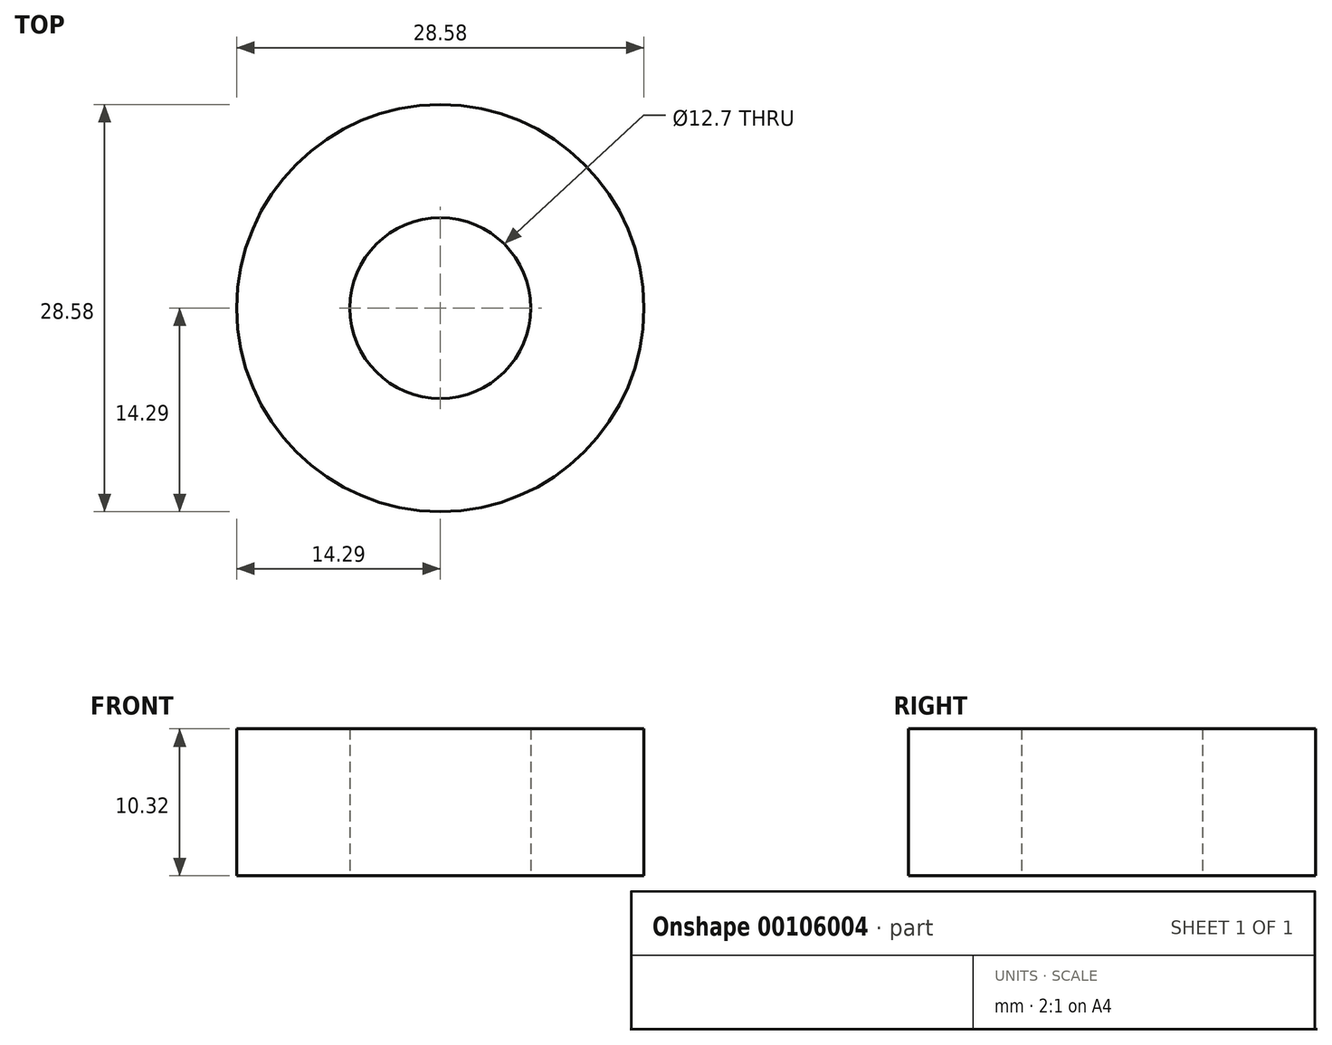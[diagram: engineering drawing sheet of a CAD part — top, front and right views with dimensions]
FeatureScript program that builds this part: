
annotation { "Feature Type Name" : "Feature", "Feature Type Description" : "" }
export const myFeature = defineFeature(function(context is Context, id is Id, definition is map)
    precondition{}
    {
        {
            var Q0;
            Q0=qCreatedBy(makeId("Top.planeOp"),FACE);
            var sketch = newSketch(context, id + "F0", { "sketchPlane" : qUnion([Q0])});
            skCircle(sketch, "E0", {"center": v(0, 0) * mm, "radius": 6.35 * mm});
            skCircle(sketch, "E1", {"center": v(0, 0) * mm, "radius": 14.29 * mm});
            skSolve(sketch);
        }
        {
            var Q0;
            Q0=makeQuery(id+"F0.imprint","IMPRINT",FACE,{"disambiguationData":[TD([[makeQuery(id+"F0.imprint","IMPRINT",EDGE,{"derivedFrom":sQuery(id+"F0.wireOp",EDGE,"E0")}),-1.0]])]});
            extrude(context, id + "F1", {"entities" : qUnion([Q0]), "depth" : 10.32 * mm});
        }
    });
